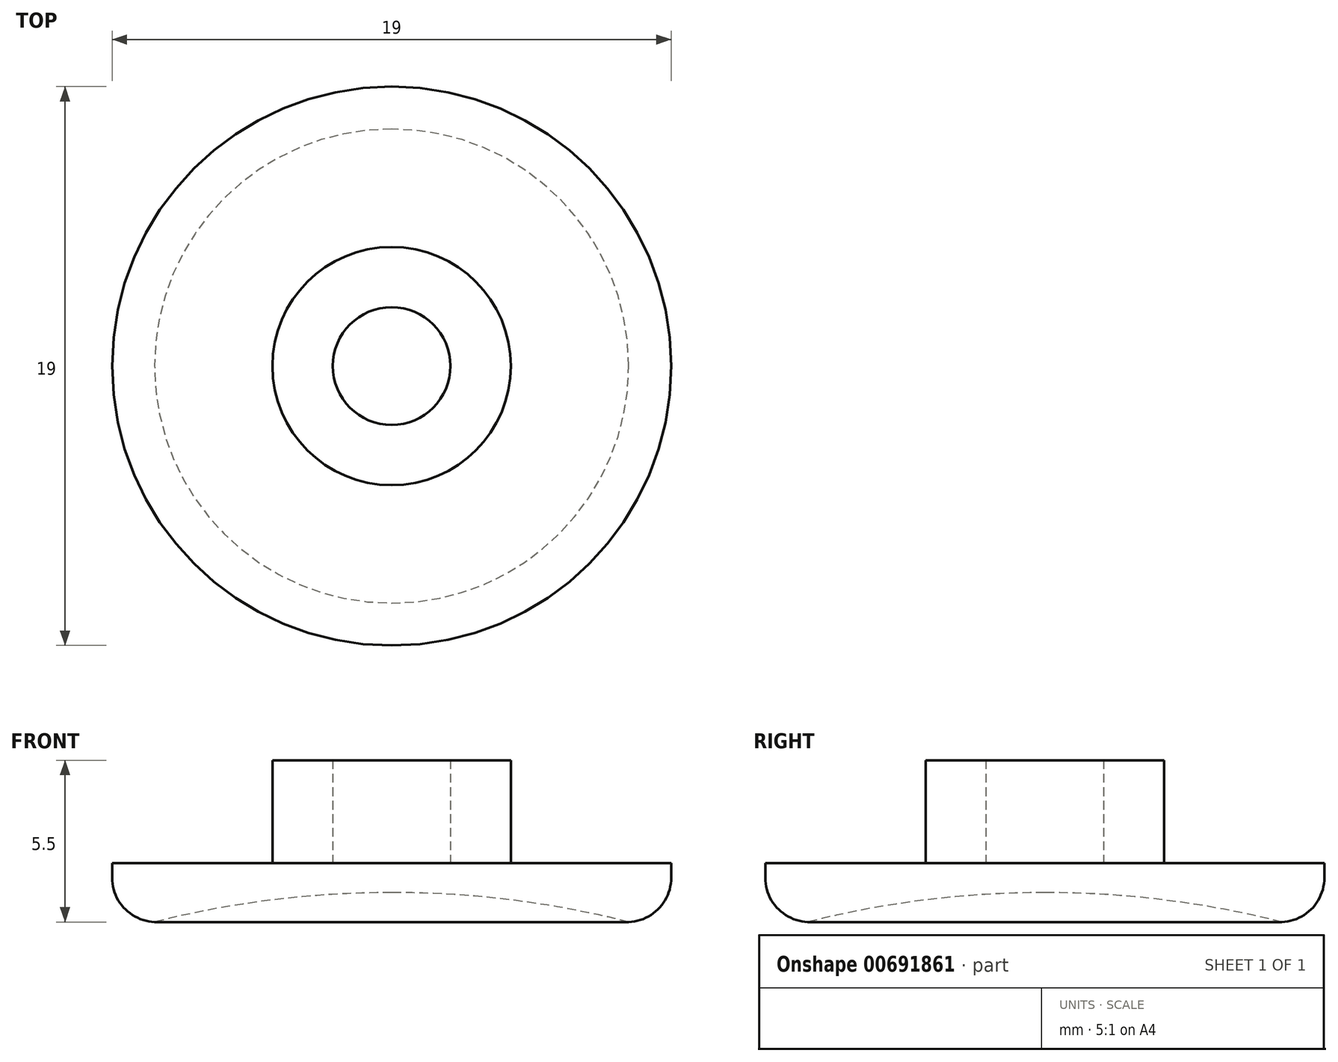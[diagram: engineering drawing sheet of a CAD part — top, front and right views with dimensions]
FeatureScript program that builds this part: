
annotation { "Feature Type Name" : "Feature", "Feature Type Description" : "" }
export const myFeature = defineFeature(function(context is Context, id is Id, definition is map)
    precondition{}
    {
        {
            var Q0;
            Q0=qCreatedBy(makeId("Top.planeOp"),FACE);
            var sketch = newSketch(context, id + "F0", { "sketchPlane" : qUnion([Q0])});
            skCircle(sketch, "E0", {"center": v(0, 0) * mm, "radius": 9.5 * mm});
            skCircle(sketch, "E1", {"center": v(0, 0) * mm, "radius": 4.05 * mm});
            skCircle(sketch, "E2", {"center": v(0, 0) * mm, "radius": 2 * mm});
            skSolve(sketch);
        }
        {
            var Q0;
            Q0=makeQuery(id+"F0.imprint","IMPRINT",FACE,{"disambiguationData":[TD([[makeQuery(id+"F0.imprint","IMPRINT",EDGE,{"derivedFrom":sQuery(id+"F0.wireOp",EDGE,"E0")}),1.0]])]});
            var Q1;
            Q1=makeQuery(id+"F0.imprint","IMPRINT",FACE,{"disambiguationData":[TD([[makeQuery(id+"F0.imprint","IMPRINT",EDGE,{"derivedFrom":sQuery(id+"F0.wireOp",EDGE,"E1")}),1.0]])]});
            var Q2;
            Q2=makeQuery(id+"F0.imprint","IMPRINT",FACE,{"disambiguationData":[TD([[makeQuery(id+"F0.imprint","IMPRINT",EDGE,{"derivedFrom":sQuery(id+"F0.wireOp",EDGE,"E2")}),1.0]])]});
            var Q3;
            Q3 = qSketchRegion(id + "F2", true);
            extrude(context, id + "F1", {"entities" : qUnion([Q0, Q1, Q2, Q3]), "depth" : 2 * mm, "offsetDistance" : 25 * mm});
        }
        {
            var Q0;
            Q0=qCreatedBy(makeId("Top.planeOp"),FACE);
            var sketch = newSketch(context, id + "F2", { "sketchPlane" : qUnion([Q0])});
            skCircle(sketch, "E3", {"center": v(0, 0) * mm, "radius": 2 * mm});
            skCircle(sketch, "E4", {"center": v(0, 0) * mm, "radius": 4.05 * mm});
            skSolve(sketch);
        }
        {
            var Q0;
            Q0 = qSketchRegion(id + "F2", true);
            extrude(context, id + "F3", {"entities" : qUnion([Q0]), "operationType" : NewBodyOperationType.ADD, "depth" : 5.5 * mm, "offsetDistance" : 25 * mm});
        }
        {
            var Q0;
            Q0=makeQuery(id+"F1.opExtrude","CAP_EDGE",EDGE,{"disambiguationData":[OSD([sQuery(id+"F0.wireOp",EDGE,"E0")])],"isStart":true});
            fillet(context, id + "F4", {"entities" : qUnion([Q0]), "radius" : 1.5 * mm, "tangentPropagation" : true, "allowEdgeOverflow" : false});
        }
        {
            var Q0;
            Q0=qCreatedBy(makeId("Front.planeOp"),FACE);
            var sketch = newSketch(context, id + "F5", { "sketchPlane" : qUnion([Q0])});
            skLineSegment(sketch, "E5", {"start": v(0, 10.26) * mm, "end": v(0, -73.29) * mm, "construction": true});
            skLineSegment(sketch, "E6", {"start": v(10.25, 0) * mm, "end": v(10.25, 1) * mm, "construction": true});
            skLineSegment(sketch, "E7", {"start": v(10.25, 1) * mm, "end": v(-10.7, 1) * mm, "construction": true});
            skArc(sketch, "E8", {"start": v(33, -32.5) * mm, "mid": v(23.51, -8.84) * mm, "end": v(0, 1) * mm});
            skPoint(sketch, "E9", {"position": v(0, 1) * mm});
            skPoint(sketch, "E10", {"position": v(0, -65) * mm});
            skArc(sketch, "E11", {"start": v(33, -32.5) * mm, "mid": v(23.16, -9.49) * mm, "end": v(0, 0) * mm});
            skPoint(sketch, "E12", {"position": v(0, -66) * mm});
            skPoint(sketch, "E13", {"position": v(0, 0) * mm});
            skLineSegment(sketch, "E14", {"start": v(0, 1) * mm, "end": v(0, 0) * mm});
            skSolve(sketch);
        }
        {
            var Q0;
            Q0=makeQuery(id+"F5.imprint","IMPRINT",FACE,{"disambiguationData":[TD([[makeQuery(id+"F5.imprint","IMPRINT",EDGE,{"derivedFrom":sQuery(id+"F5.wireOp",EDGE,"E8")}),1.0]])]});
            var Q1;
            Q1=sQuery(id+"F5.wireOp",EDGE,"E5");
            revolve(context, id + "F6", {"operationType" : NewBodyOperationType.REMOVE, "entities" : qUnion([Q0]), "axis" : qUnion([Q1]), "revolveType" : RevolveType.FULL});
        }
    });
